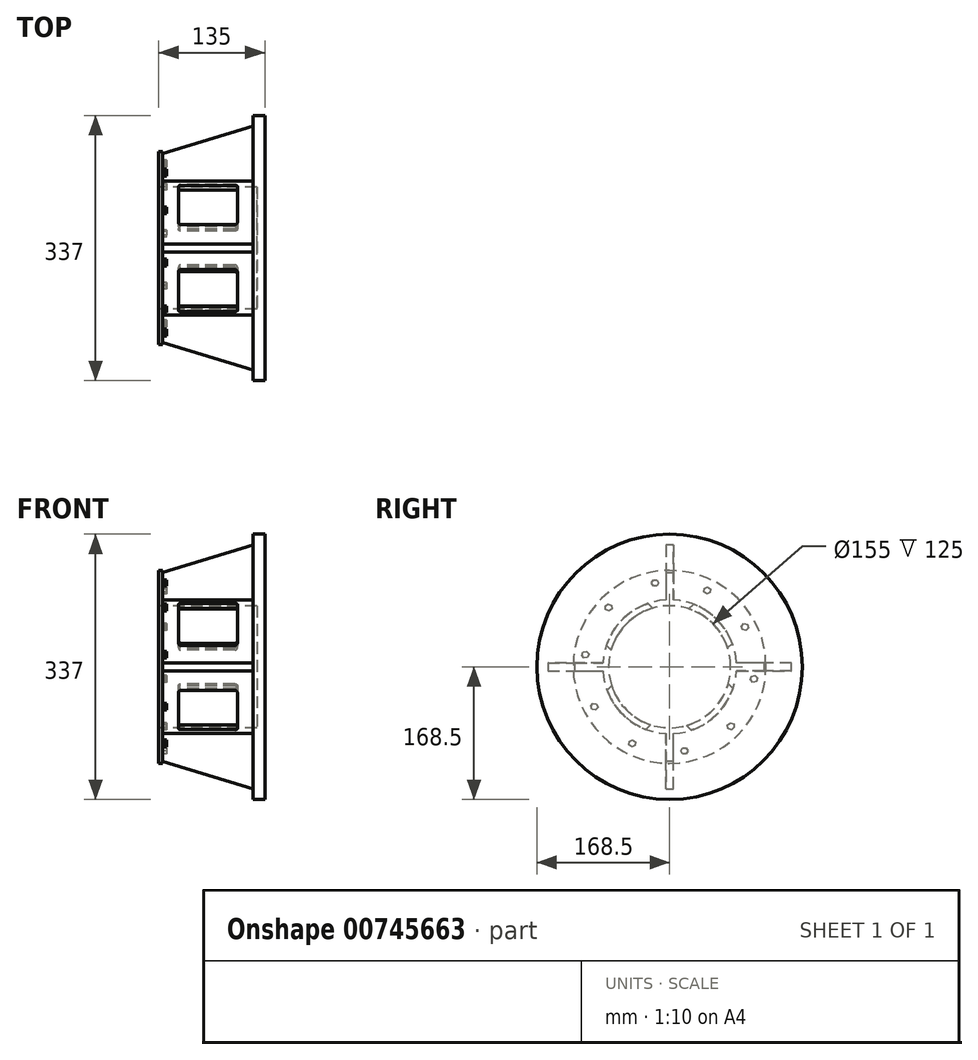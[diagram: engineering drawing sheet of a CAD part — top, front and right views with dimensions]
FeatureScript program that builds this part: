
annotation { "Feature Type Name" : "Feature", "Feature Type Description" : "" }
export const myFeature = defineFeature(function(context is Context, id is Id, definition is map)
    precondition{}
    {
        {
            var Q0;
            Q0=qCreatedBy(makeId("Right.planeOp"),FACE);
            var sketch = newSketch(context, id + "F0", { "sketchPlane" : qUnion([Q0])});
            skCircle(sketch, "E0", {"center": v(0, 0) * mm, "radius": 122.5 * mm});
            skCircle(sketch, "E1", {"center": v(0, 0) * mm, "radius": 85 * mm});
            skCircle(sketch, "E2", {"center": v(0, 0) * mm, "radius": 168.5 * mm});
            skSolve(sketch);
        }
        {
            var Q0;
            Q0=makeQuery(id+"F0.imprint","IMPRINT",FACE,{"disambiguationData":[TD([[makeQuery(id+"F0.imprint","IMPRINT",EDGE,{"derivedFrom":sQuery(id+"F0.wireOp",EDGE,"E1")}),1.0]])]});
            var Q1;
            Q1=sQuery(id+"F0.wireOp",EDGE,"E0");
            extrude(context, id + "F1", {"entities" : qUnion([Q0]), "surfaceEntities" : qUnion([Q1]), "depth" : 135 * mm, "offsetDistance" : 25 * mm});
        }
        {
            var Q0;
            Q0=makeQuery(id+"F0.imprint","IMPRINT",FACE,{"disambiguationData":[TD([[makeQuery(id+"F0.imprint","IMPRINT",EDGE,{"derivedFrom":sQuery(id+"F0.wireOp",EDGE,"E0")}),1.0]])]});
            extrude(context, id + "F2", {"entities" : qUnion([Q0]), "operationType" : NewBodyOperationType.ADD, "depth" : 5 * mm, "offsetDistance" : 25 * mm});
        }
        {
            var Q0;
            Q0=makeQuery(id+"F1.opExtrude","CAP_FACE",FACE,{"disambiguationData":[OSD([sQuery(id+"F0.wireOp",EDGE,"E1")])],"isStart":false});
            var sketch = newSketch(context, id + "F3", { "sketchPlane" : qUnion([Q0])});
            skCircle(sketch, "E3.0.0", {"center": v(0, 0) * mm, "radius": 168.5 * mm});
            skSolve(sketch);
        }
        {
            var Q0;
            Q0=makeQuery(id+"F3.imprint","IMPRINT",FACE,{"disambiguationData":[TD([[makeQuery(id+"F3.imprint","IMPRINT",EDGE,{"derivedFrom":sQuery(id+"F3.wireOp",EDGE,"E3.0.0")}),1.0]])]});
            var Q1;
            Q1=makeQuery(id+"F3.imprint","IMPRINT",FACE,{"disambiguationData":[TD([[makeQuery(id+"F3.imprint","IMPRINT",EDGE,{"derivedFrom":makeQuery(id+"F1.opExtrude","CAP_EDGE",EDGE,{"disambiguationData":[OSD([sQuery(id+"F0.wireOp",EDGE,"E1")])],"isStart":false})}),1.0]])]});
            extrude(context, id + "F4", {"entities" : qUnion([Q0, Q1]), "operationType" : NewBodyOperationType.ADD, "oppositeDirection" : true, "depth" : 15 * mm, "offsetDistance" : 25 * mm});
        }
        {
            var Q0;
            Q0=makeQuery(id+"F4.opExtrude","CAP_FACE",FACE,{"disambiguationData":[OSD([sQuery(id+"F3.wireOp",EDGE,"E3.0.0")])],"isStart":false});
            var sketch = newSketch(context, id + "F5", { "sketchPlane" : qUnion([Q0])});
            skArc(sketch, "E4.0", {"start": v(5, 84.85) * mm, "mid": v(0, 85) * mm, "end": v(-5, 84.85) * mm});
            skLineSegment(sketch, "E5", {"start": v(-5, 84.85) * mm, "end": v(-5, 154.85) * mm});
            skLineSegment(sketch, "E6", {"start": v(-5, 154.85) * mm, "end": v(5, 154.85) * mm});
            skLineSegment(sketch, "E7", {"start": v(5, 154.85) * mm, "end": v(5, 84.85) * mm});
            skSolve(sketch);
        }
        {
            var Q0;
            Q0=makeQuery(id+"F2.opExtrude","CAP_FACE",FACE,{"disambiguationData":[OSD([sQuery(id+"F0.wireOp",EDGE,"E0"),sQuery(id+"F0.wireOp",EDGE,"E1")])],"isStart":false});
            var sketch = newSketch(context, id + "F6", { "sketchPlane" : qUnion([Q0])});
            skArc(sketch, "E8.0", {"start": v(5, 84.85) * mm, "mid": v(0, 85) * mm, "end": v(-5, 84.85) * mm});
            skLineSegment(sketch, "E9.bottom", {"start": v(-5, 120) * mm, "end": v(5, 120) * mm});
            skLineSegment(sketch, "E9.top", {"start": v(-5, 80) * mm, "end": v(5, 80) * mm});
            skLineSegment(sketch, "E9.left", {"start": v(-5, 120) * mm, "end": v(-5, 80) * mm});
            skLineSegment(sketch, "E9.right", {"start": v(5, 120) * mm, "end": v(5, 80) * mm});
            skSolve(sketch);
        }
        {
            var Q1;
            Q1=makeQuery(id+"F5.imprint","IMPRINT",FACE,{"disambiguationData":[TD([[makeQuery(id+"F5.imprint","IMPRINT",EDGE,{"derivedFrom":sQuery(id+"F5.wireOp",EDGE,"E4.0")}),1.0]])]});
            var Q2;
            {var subQ0=sQuery(id+"F6.wireOp",EDGE,"E8.0");Q2=makeQuery(id+"F6.imprint","IMPRINT",FACE,{"disambiguationData":[TD([[makeQuery(id+"F6.imprint","IMPRINT",EDGE,{"derivedFrom":subQ0}),-1.0]])]});}
            loft(context, id + "F7", {"operationType" : NewBodyOperationType.ADD, "sheetProfilesArray" : [{ "sheetProfileEntities" : qUnion([Q1]) }, { "sheetProfileEntities" : qUnion([Q2]) }]});
        }
        {
            var Q0;
            Q0=makeQuery(id+"F1.opExtrude","SWEPT_BODY",BODY,{"disambiguationData":[OSD([sQuery(id+"F0.wireOp",EDGE,"E1")])]});
            var Q1;
            Q1=makeQuery(id+"F1.opExtrude","SWEPT_FACE",FACE,{"disambiguationData":[OSD([sQuery(id+"F0.wireOp",EDGE,"E1")])]});
            circularPattern(context, id + "F8", {"operationType" : NewBodyOperationType.ADD, "entities" : qUnion([Q0]), "axis" : qUnion([Q1]), "angle" : 360 * degree, "instanceCount" : 4, "equalSpace" : true});
        }
        {
            var Q0;
            Q0=makeQuery(id+"F2.opExtrude","CAP_FACE",FACE,{"disambiguationData":[OSD([sQuery(id+"F0.wireOp",EDGE,"E0"),sQuery(id+"F0.wireOp",EDGE,"E1")])],"isStart":false});
            var sketch = newSketch(context, id + "F9", { "sketchPlane" : qUnion([Q0])});
            skCircle(sketch, "E10.cCircle", {"center": v(-18.54, 106.66) * mm, "radius": 3.9 * mm, "construction": true});
            skLineSegment(sketch, "E10.0", {"start": v(-16.3, 102.77) * mm, "end": v(-20.79, 102.77) * mm});
            skLineSegment(sketch, "E10.1", {"start": v(-20.79, 102.77) * mm, "end": v(-23.04, 106.66) * mm});
            skLineSegment(sketch, "E10.2", {"start": v(-23.04, 106.66) * mm, "end": v(-20.79, 110.56) * mm});
            skLineSegment(sketch, "E10.3", {"start": v(-20.79, 110.56) * mm, "end": v(-16.3, 110.56) * mm});
            skLineSegment(sketch, "E10.4", {"start": v(-16.3, 110.56) * mm, "end": v(-14.04, 106.66) * mm});
            skLineSegment(sketch, "E10.5", {"start": v(-14.04, 106.66) * mm, "end": v(-16.3, 102.77) * mm});
            skPoint(sketch, "E10.0.midPoint", {"position": v(-18.54, 102.77) * mm});
            skLineSegment(sketch, "E11.1.0", {"start": v(-74.06, 78.04) * mm, "end": v(-73.59, 73.57) * mm});
            skLineSegment(sketch, "E11.1.1", {"start": v(-77.23, 70.92) * mm, "end": v(-81.33, 72.75) * mm});
            skLineSegment(sketch, "E11.1.2", {"start": v(-81.8, 77.22) * mm, "end": v(-78.17, 79.87) * mm});
            skPoint(sketch, "E11.1.3", {"position": v(-75.4, 72.24) * mm});
            skCircle(sketch, "E11.1.4", {"center": v(-77.7, 75.4) * mm, "radius": 3.9 * mm, "construction": true});
            skLineSegment(sketch, "E11.1.5", {"start": v(-81.33, 72.75) * mm, "end": v(-81.8, 77.22) * mm});
            skLineSegment(sketch, "E11.1.6", {"start": v(-78.17, 79.87) * mm, "end": v(-74.06, 78.04) * mm});
            skLineSegment(sketch, "E11.1.7", {"start": v(-73.59, 73.57) * mm, "end": v(-77.23, 70.92) * mm});
            skLineSegment(sketch, "E11.2.0", {"start": v(-105.78, 19.6) * mm, "end": v(-102.77, 16.26) * mm});
            skLineSegment(sketch, "E11.2.1", {"start": v(-104.16, 11.99) * mm, "end": v(-108.56, 11.05) * mm});
            skLineSegment(sketch, "E11.2.2", {"start": v(-111.57, 14.4) * mm, "end": v(-110.18, 18.67) * mm});
            skPoint(sketch, "E11.2.3", {"position": v(-103.47, 14.12) * mm});
            skCircle(sketch, "E11.2.4", {"center": v(-107.17, 15.33) * mm, "radius": 3.9 * mm, "construction": true});
            skLineSegment(sketch, "E11.2.5", {"start": v(-108.56, 11.05) * mm, "end": v(-111.57, 14.4) * mm});
            skLineSegment(sketch, "E11.2.6", {"start": v(-110.18, 18.67) * mm, "end": v(-105.78, 19.6) * mm});
            skLineSegment(sketch, "E11.2.7", {"start": v(-102.77, 16.26) * mm, "end": v(-104.16, 11.99) * mm});
            skLineSegment(sketch, "E11.3.0", {"start": v(-97.1, -46.32) * mm, "end": v(-92.7, -47.25) * mm});
            skLineSegment(sketch, "E11.3.1", {"start": v(-91.32, -51.53) * mm, "end": v(-94.33, -54.87) * mm});
            skLineSegment(sketch, "E11.3.2", {"start": v(-98.72, -53.94) * mm, "end": v(-100.11, -49.66) * mm});
            skPoint(sketch, "E11.3.3", {"position": v(-92.01, -49.4) * mm});
            skCircle(sketch, "E11.3.4", {"center": v(-95.71, -50.6) * mm, "radius": 3.9 * mm, "construction": true});
            skLineSegment(sketch, "E11.3.5", {"start": v(-94.33, -54.87) * mm, "end": v(-98.72, -53.94) * mm});
            skLineSegment(sketch, "E11.3.6", {"start": v(-100.11, -49.66) * mm, "end": v(-97.1, -46.32) * mm});
            skLineSegment(sketch, "E11.3.7", {"start": v(-92.7, -47.25) * mm, "end": v(-91.32, -51.53) * mm});
            skLineSegment(sketch, "E11.4.0", {"start": v(-51.33, -94.55) * mm, "end": v(-47.23, -92.72) * mm});
            skLineSegment(sketch, "E11.4.1", {"start": v(-43.59, -95.36) * mm, "end": v(-44.06, -99.83) * mm});
            skLineSegment(sketch, "E11.4.2", {"start": v(-48.17, -101.66) * mm, "end": v(-51.8, -99.02) * mm});
            skPoint(sketch, "E11.4.3", {"position": v(-45.4, -94.04) * mm});
            skCircle(sketch, "E11.4.4", {"center": v(-47.7, -97.2) * mm, "radius": 3.9 * mm, "construction": true});
            skLineSegment(sketch, "E11.4.5", {"start": v(-44.06, -99.83) * mm, "end": v(-48.17, -101.66) * mm});
            skLineSegment(sketch, "E11.4.6", {"start": v(-51.8, -99.02) * mm, "end": v(-51.33, -94.55) * mm});
            skLineSegment(sketch, "E11.4.7", {"start": v(-47.23, -92.72) * mm, "end": v(-43.59, -95.36) * mm});
            skLineSegment(sketch, "E11.5.0", {"start": v(14.04, -106.66) * mm, "end": v(16.3, -102.77) * mm});
            skLineSegment(sketch, "E11.5.1", {"start": v(20.79, -102.77) * mm, "end": v(23.04, -106.66) * mm});
            skLineSegment(sketch, "E11.5.2", {"start": v(20.79, -110.56) * mm, "end": v(16.3, -110.56) * mm});
            skPoint(sketch, "E11.5.3", {"position": v(18.54, -102.77) * mm});
            skCircle(sketch, "E11.5.4", {"center": v(18.54, -106.66) * mm, "radius": 3.9 * mm, "construction": true});
            skLineSegment(sketch, "E11.5.5", {"start": v(23.04, -106.66) * mm, "end": v(20.79, -110.56) * mm});
            skLineSegment(sketch, "E11.5.6", {"start": v(16.3, -110.56) * mm, "end": v(14.04, -106.66) * mm});
            skLineSegment(sketch, "E11.5.7", {"start": v(16.3, -102.77) * mm, "end": v(20.79, -102.77) * mm});
            skLineSegment(sketch, "E11.6.0", {"start": v(74.06, -78.04) * mm, "end": v(73.59, -73.57) * mm});
            skLineSegment(sketch, "E11.6.1", {"start": v(77.23, -70.92) * mm, "end": v(81.33, -72.75) * mm});
            skLineSegment(sketch, "E11.6.2", {"start": v(81.8, -77.22) * mm, "end": v(78.17, -79.87) * mm});
            skPoint(sketch, "E11.6.3", {"position": v(75.4, -72.24) * mm});
            skCircle(sketch, "E11.6.4", {"center": v(77.7, -75.4) * mm, "radius": 3.9 * mm, "construction": true});
            skLineSegment(sketch, "E11.6.5", {"start": v(81.33, -72.75) * mm, "end": v(81.8, -77.22) * mm});
            skLineSegment(sketch, "E11.6.6", {"start": v(78.17, -79.87) * mm, "end": v(74.06, -78.04) * mm});
            skLineSegment(sketch, "E11.6.7", {"start": v(73.59, -73.57) * mm, "end": v(77.23, -70.92) * mm});
            skLineSegment(sketch, "E11.7.0", {"start": v(105.78, -19.6) * mm, "end": v(102.77, -16.26) * mm});
            skLineSegment(sketch, "E11.7.1", {"start": v(104.16, -11.99) * mm, "end": v(108.56, -11.05) * mm});
            skLineSegment(sketch, "E11.7.2", {"start": v(111.57, -14.4) * mm, "end": v(110.18, -18.67) * mm});
            skPoint(sketch, "E11.7.3", {"position": v(103.47, -14.12) * mm});
            skCircle(sketch, "E11.7.4", {"center": v(107.17, -15.33) * mm, "radius": 3.9 * mm, "construction": true});
            skLineSegment(sketch, "E11.7.5", {"start": v(108.56, -11.05) * mm, "end": v(111.57, -14.4) * mm});
            skLineSegment(sketch, "E11.7.6", {"start": v(110.18, -18.67) * mm, "end": v(105.78, -19.6) * mm});
            skLineSegment(sketch, "E11.7.7", {"start": v(102.77, -16.26) * mm, "end": v(104.16, -11.99) * mm});
            skLineSegment(sketch, "E11.8.0", {"start": v(97.1, 46.32) * mm, "end": v(92.7, 47.25) * mm});
            skLineSegment(sketch, "E11.8.1", {"start": v(91.32, 51.53) * mm, "end": v(94.33, 54.87) * mm});
            skLineSegment(sketch, "E11.8.2", {"start": v(98.72, 53.94) * mm, "end": v(100.11, 49.66) * mm});
            skPoint(sketch, "E11.8.3", {"position": v(92.01, 49.4) * mm});
            skCircle(sketch, "E11.8.4", {"center": v(95.71, 50.6) * mm, "radius": 3.9 * mm, "construction": true});
            skLineSegment(sketch, "E11.8.5", {"start": v(94.33, 54.87) * mm, "end": v(98.72, 53.94) * mm});
            skLineSegment(sketch, "E11.8.6", {"start": v(100.11, 49.66) * mm, "end": v(97.1, 46.32) * mm});
            skLineSegment(sketch, "E11.8.7", {"start": v(92.7, 47.25) * mm, "end": v(91.32, 51.53) * mm});
            skLineSegment(sketch, "E11.9.0", {"start": v(51.33, 94.55) * mm, "end": v(47.23, 92.72) * mm});
            skLineSegment(sketch, "E11.9.1", {"start": v(43.59, 95.36) * mm, "end": v(44.06, 99.83) * mm});
            skLineSegment(sketch, "E11.9.2", {"start": v(48.17, 101.66) * mm, "end": v(51.8, 99.02) * mm});
            skPoint(sketch, "E11.9.3", {"position": v(45.4, 94.04) * mm});
            skCircle(sketch, "E11.9.4", {"center": v(47.7, 97.2) * mm, "radius": 3.9 * mm, "construction": true});
            skLineSegment(sketch, "E11.9.5", {"start": v(44.06, 99.83) * mm, "end": v(48.17, 101.66) * mm});
            skLineSegment(sketch, "E11.9.6", {"start": v(51.8, 99.02) * mm, "end": v(51.33, 94.55) * mm});
            skLineSegment(sketch, "E11.9.7", {"start": v(47.23, 92.72) * mm, "end": v(43.59, 95.36) * mm});
            skPoint(sketch, "E11.center", {"position": v(0, 0) * mm});
            skSolve(sketch);
        }
        {
            var Q0;
            Q0 = qSketchRegion(id + "F9", true);
            extrude(context, id + "F10", {"entities" : qUnion([Q0]), "operationType" : NewBodyOperationType.ADD, "depth" : 5 * mm, "offsetDistance" : 25 * mm});
        }
        {
            var Q0;
            {var subQ0=sQuery(id+"F0.wireOp",EDGE,"E1");Q0=makeQuery(id+"F2.boolean.opBoolean","MERGE",FACE,{"derivedFrom":[makeQuery(id+"F1.opExtrude","CAP_FACE",FACE,{"disambiguationData":[OSD([subQ0])],"isStart":true}),makeQuery(id+"F2.opExtrude","CAP_FACE",FACE,{"disambiguationData":[OSD([sQuery(id+"F0.wireOp",EDGE,"E0"),subQ0])],"isStart":true})]});}
            var sketch = newSketch(context, id + "F11", { "sketchPlane" : qUnion([Q0])});
            skCircle(sketch, "E12", {"center": v(0, 0) * mm, "radius": 77.5 * mm});
            skSolve(sketch);
        }
        {
            var Q0;
            Q0=makeQuery(id+"F11.imprint","IMPRINT",FACE,{"disambiguationData":[TD([[makeQuery(id+"F11.imprint","IMPRINT",EDGE,{"derivedFrom":sQuery(id+"F11.wireOp",EDGE,"E12")}),1.0]])]});
            extrude(context, id + "F12", {"entities" : qUnion([Q0]), "operationType" : NewBodyOperationType.REMOVE, "oppositeDirection" : true, "depth" : 125 * mm, "offsetDistance" : 25 * mm});
        }
        {
            var Q0;
            Q0=qCreatedBy(makeId("Top.planeOp"),FACE);
            var Q1;
            Q1=qCreatedBy(makeId("Front.planeOp"),FACE);
            cPlane(context, id + "F13", {"entities" : qUnion([Q0, Q1]), "cplaneType" : CPlaneType.MID_PLANE, "offset" : 25 * mm, "width" : 150 * mm, "height" : 150 * mm});
        }
        {
            var Q0;
            Q0=qCreatedBy(id+"F13.planeOp",FACE);
            var sketch = newSketch(context, id + "F14", { "sketchPlane" : qUnion([Q0])});
            skLineSegment(sketch, "E13.bottom", {"start": v(-97, 35) * mm, "end": v(-28, 35) * mm});
            skLineSegment(sketch, "E13.top", {"start": v(-97, -35) * mm, "end": v(-28, -35) * mm});
            skLineSegment(sketch, "E13.left", {"start": v(-100, 32) * mm, "end": v(-100, -32) * mm});
            skLineSegment(sketch, "E13.right", {"start": v(-25, 32) * mm, "end": v(-25, -32) * mm});
            skPoint(sketch, "E14.visualSharp", {"position": v(-100, 35) * mm});
            skArc(sketch, "E14.filletArc", {"start": v(-97, 35) * mm, "mid": v(-99.12, 34.12) * mm, "end": v(-100, 32) * mm});
            skPoint(sketch, "E15.visualSharp", {"position": v(-100, -35) * mm});
            skArc(sketch, "E15.filletArc", {"start": v(-100, -32) * mm, "mid": v(-99.12, -34.12) * mm, "end": v(-97, -35) * mm});
            skPoint(sketch, "E16.visualSharp", {"position": v(-25, -35) * mm});
            skArc(sketch, "E16.filletArc", {"start": v(-28, -35) * mm, "mid": v(-25.88, -34.12) * mm, "end": v(-25, -32) * mm});
            skPoint(sketch, "E17.visualSharp", {"position": v(-25, 35) * mm});
            skArc(sketch, "E17.filletArc", {"start": v(-25, 32) * mm, "mid": v(-25.88, 34.12) * mm, "end": v(-28, 35) * mm});
            skSolve(sketch);
        }
        {
            var Q0;
            Q0 = qSketchRegion(id + "F14", true);
            extrude(context, id + "F15", {"entities" : qUnion([Q0]), "operationType" : NewBodyOperationType.REMOVE, "endBound" : BoundingType.SYMMETRIC, "oppositeDirection" : true, "depth" : 200 * mm, "offsetDistance" : 25 * mm});
        }
        {
            var Q0;
            Q0=qCreatedBy(makeId("Front.planeOp"),FACE);
            var Q1;
            Q1=qCreatedBy(makeId("Top.planeOp"),FACE);
            cPlane(context, id + "F16", {"entities" : qUnion([Q0, Q1]), "cplaneType" : CPlaneType.MID_PLANE, "offset" : 25 * mm, "flipAlignment" : true, "width" : 150 * mm, "height" : 150 * mm});
        }
        {
            var Q0;
            Q0=qCreatedBy(id+"F16.planeOp",FACE);
            var sketch = newSketch(context, id + "F17", { "sketchPlane" : qUnion([Q0])});
            skLineSegment(sketch, "E18.bottom", {"start": v(97, 37.5) * mm, "end": v(28, 37.5) * mm});
            skLineSegment(sketch, "E18.top", {"start": v(97, -37.5) * mm, "end": v(28, -37.5) * mm});
            skLineSegment(sketch, "E18.left", {"start": v(100, 34.5) * mm, "end": v(100, -34.5) * mm});
            skLineSegment(sketch, "E18.right", {"start": v(25, 34.5) * mm, "end": v(25, -34.5) * mm});
            skPoint(sketch, "E19.visualSharp", {"position": v(100, 37.5) * mm});
            skArc(sketch, "E19.filletArc", {"start": v(100, 34.5) * mm, "mid": v(99.12, 36.62) * mm, "end": v(97, 37.5) * mm});
            skPoint(sketch, "E20.visualSharp", {"position": v(25, 37.5) * mm});
            skArc(sketch, "E20.filletArc", {"start": v(28, 37.5) * mm, "mid": v(25.88, 36.62) * mm, "end": v(25, 34.5) * mm});
            skPoint(sketch, "E21.visualSharp", {"position": v(25, -37.5) * mm});
            skArc(sketch, "E21.filletArc", {"start": v(25, -34.5) * mm, "mid": v(25.88, -36.62) * mm, "end": v(28, -37.5) * mm});
            skPoint(sketch, "E22.visualSharp", {"position": v(100, -37.5) * mm});
            skArc(sketch, "E22.filletArc", {"start": v(97, -37.5) * mm, "mid": v(99.12, -36.62) * mm, "end": v(100, -34.5) * mm});
            skSolve(sketch);
        }
        {
            var Q0;
            Q0 = qSketchRegion(id + "F17", true);
            extrude(context, id + "F18", {"entities" : qUnion([Q0]), "operationType" : NewBodyOperationType.REMOVE, "endBound" : BoundingType.SYMMETRIC, "oppositeDirection" : true, "depth" : 200 * mm, "offsetDistance" : 25 * mm});
        }
    });
